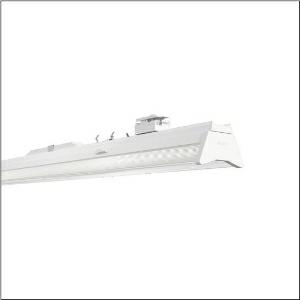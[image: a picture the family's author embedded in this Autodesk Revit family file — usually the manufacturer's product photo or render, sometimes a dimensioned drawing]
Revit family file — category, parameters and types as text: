
# Revit family: licross_21_performance_mo_51td16vn445g
name_source: partatom
category: Lighting Fixtures
units: mm (PartAtom-declared; Revit-internal decimal feet)

## family parameters
Cut with Voids When Loaded = No
Host = Face
Light Source = No
Part Type = Normal
Room Calculation Point = No
Round Connector Dimension = Use Diameter
Shared = No

## types (1)
- --- (1 x LED, 4500 lm, 24.2 W, 4000K)
    Apparent Load = 24 VA
    CIE Flux Codes = 66 88 96 79 100
    Color Rendering = 80
    Color Temperature = 4000K
    Default Elevation = 1800 mm
    Description = Licross 21 Performance MO, luminaire insert, of sheet steel, galvanised, coil coated, white, length: 1.500mm, width: 120mm, height: 123mm, LED rated luminous flux: 4.500lm, light colour: 840, SDCM (Standard Deviation of Colour Matching)MacAdam ≤ 2 SDCM (initial), control gear: DALI 2, CLO, with plug, 5-pole, with phase selection, mains connection: 220..240V, AC, 50/60Hz, start of lifetime: 24W, end of service life: 26W, internal wiring halogen-free, primary light control with lens, of plastic, primary optical cover: cover, of PMMA, light emission: direct/indirect distribution, primary light characteristic: symmetric, protection rating (complete): IP54, insulation class (complete): insulation class I (protective earthing), certification: CE, ENEC, VDE, UKCA, protection symbol: D if used in an environment with non-conductive dust loads with corresponding accessories, impact resistance: IK06, permissible ambient temperature for indoor applications: -25..+45°C, corresponds to IFS (International Featured Standards) requirements for safety and quality in the food industry, reducing of maximum allowable ambient temperature of 5°C with ceiling mounting, LABS conformity tested according to VDMA 24364:2018-05, The light source and the operating device comply with the requirements of the Ecodesign Regulation (EU) 2019/2020 and are replaceable in accordance with this regulation, packaging unit: 1 piece
    Height = 114 mm
    Lamp = 1 x LED
    Lamp Light Flux = 4500 lm
    Lamp Power = 24.2 W
    Lamp count = 1
    Length = 1500 mm
    Luminous efficacy = 186 lm/W
    Manufacturer = Siteco
    ModVariant = No
    Model = 51TD16VN445G
    Mounting Place = Ceiling
    Mounting Type = Pendant
    Number of Poles = 1
    OnlyDefault = Yes
    Power Factor = 1
    Product Name = Licross 21 Performance MO
    Product group = luminaire insert | ceiling pendant
    ProductGroupID = 901
    Protection Class = Protection class I
    Protection Degree = IP 54
    RLX_Detail_Level = 1
    RLX_Emergency_Light_Flux = 0 lm
    RLX_Emergency_Type = 0
    RLX_Emergency_Type_DB = No
    RlxData = <blob elided: 34085 chars, md5=a113bde3>
    Socket = socket
    Standby Power = 0 W
    System Light Flux = 4500 lm
    System Power = 24 W
    Type Comments = factory setting: luminous flux: 100 % | dim-lin: 254 | 160 mA
    Type Image = l_1256138.jpg
    URL = http://relux.com
    VarID = @adj_056503
    Voltage = 0 V
    Weight = 0.00 kg
    Width = 120 mm

## geometry (parser evidence)
native form markers: Blend x4, Sweep x11
no freeform markers — native parametric forms only
